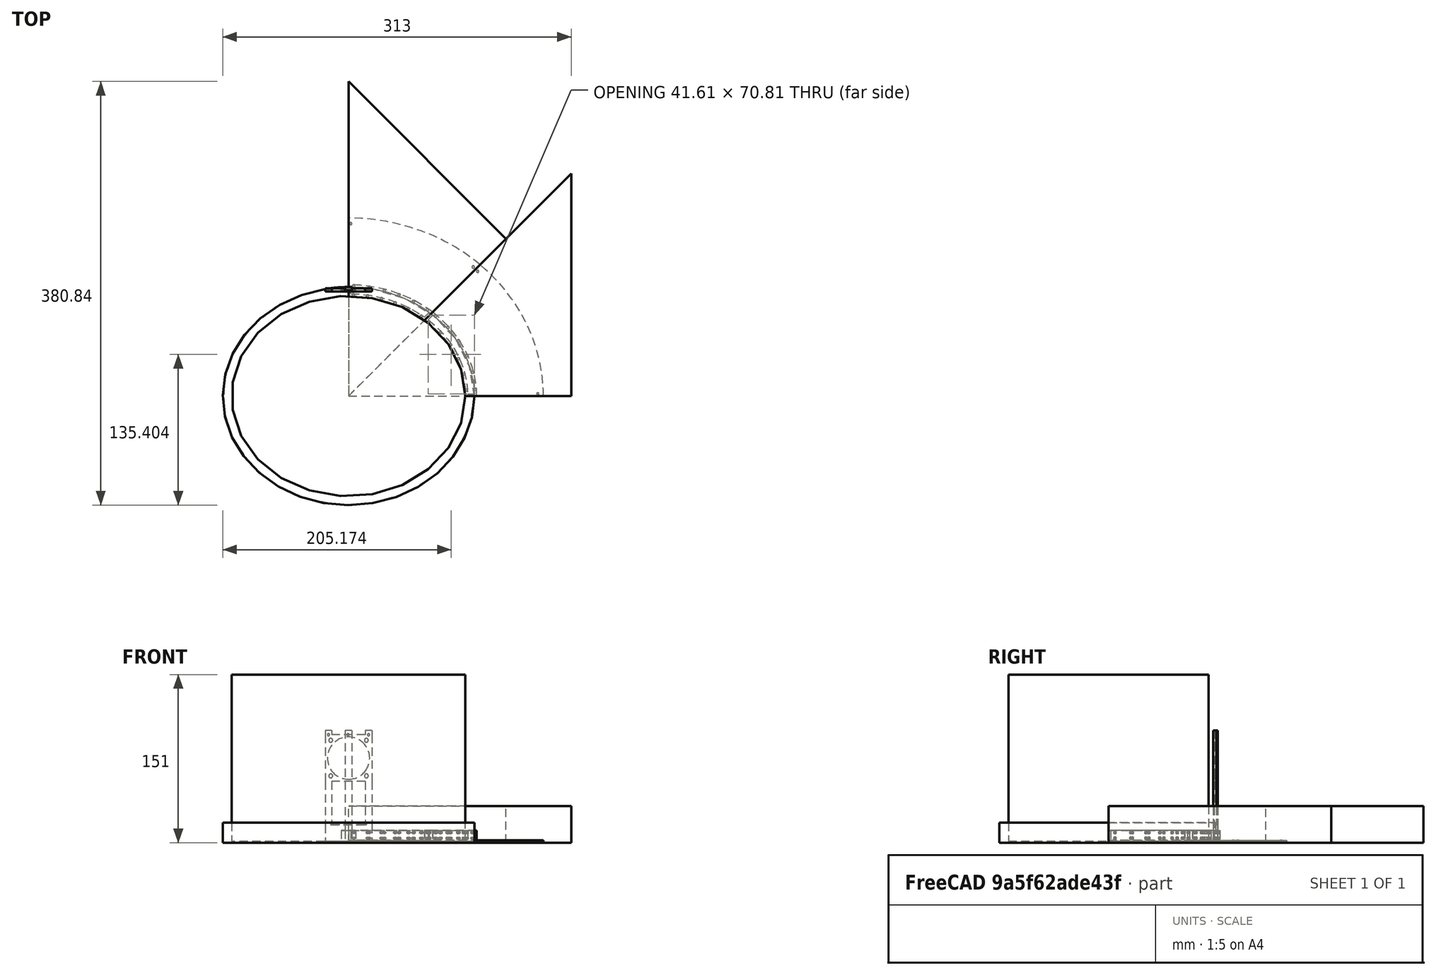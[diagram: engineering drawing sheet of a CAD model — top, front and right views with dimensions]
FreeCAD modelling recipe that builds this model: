
FCSTD DOCUMENT  (FreeCAD 0.14R3702 (Git))
Label: sun-hat-2
License: CC-BY 3.0
LicenseURL: http://creativecommons.org/licenses/by/3.0/
objects: Part::Cut×41, Part::Feature×16, Part::Cylinder×14, Part::Box×12, Part::Extrusion×8, Part::Fuse×6, Part::Ellipse×5, Part::MultiCommon×4, App::DocumentObjectGroup×1
note: 106 computed .brp shape members not serialized (recipe doc carries the construction recipe); baked Part::Feature solids carry a one-line shape summary decoded from their .brp

FEATURE [Part::Ellipse] Ellipse
  Angle0 = 0
  Angle1 = 360
  MajorRadius = 105
  MinorRadius = 90
FEATURE [Part::Ellipse] Ellipse001
  Angle0 = 0
  Angle1 = 360
  MajorRadius = 107
  MinorRadius = 92
FEATURE [Part::Ellipse] Ellipse002
  Angle0 = 0
  Angle1 = 360
  MajorRadius = 113
  MinorRadius = 98
FEATURE [Part::Ellipse] Ellipse003
  Angle0 = 0
  Angle1 = 360
  MajorRadius = 115
  MinorRadius = 100
FEATURE [Part::Feature] Face
  shape: bbox 210 x 180 x 2e-07 mm, 1 faces, 0 solids (baked)
FEATURE [Part::Feature] Face001
  shape: bbox 214 x 184 x 2e-07 mm, 1 faces, 0 solids (baked)
FEATURE [Part::Feature] Face002
  shape: bbox 226 x 196 x 2e-07 mm, 1 faces, 0 solids (baked)
FEATURE [Part::Feature] Face003
  shape: bbox 230 x 200 x 2e-07 mm, 1 faces, 0 solids (baked)
FEATURE [Part::Extrusion] Extrude  label="innermost+"
  Base = -> Face001
  Dir = (0,0,20)
  Placement = pos=(0,0,-1) rot=(0,0,1;0rad)
  Solid = false
FEATURE [Part::Extrusion] Extrude001  label="outermost-"
  Base = -> Face002
  Dir = (0,0,18)
  Solid = false
FEATURE [Part::Extrusion] Extrude002  label="innermost"
  Base = -> Face
  Dir = (0,0,150)
  Placement = pos=(0,0,-1) rot=(0,0,1;0rad)
  Solid = false
FEATURE [Part::Extrusion] Extrude003  label="outermost"
  Base = -> Face003
  Dir = (0,0,10)
  Solid = false
FEATURE [Part::Extrusion] Extrude004  label="central ellipse"
  Base = -> Face
  Dir = (0,0,150)
  Solid = false
FEATURE [Part::Cylinder] Cylinder
  Angle = 360
  Height = 150
  Placement = pos=(0,0,8) rot=(0,1,0;1.5708rad)
  Radius = 1
FEATURE [Part::Cylinder] Cylinder001
  Angle = 360
  Height = 150
  Placement = pos=(0,0,3) rot=(0,1,0;1.5708rad)
  Radius = 1
FEATURE [Part::Ellipse] Ellipse004
  Angle0 = 0
  Angle1 = 360
  MajorRadius = 175
  MinorRadius = 160
FEATURE [Part::Feature] Face004
  shape: bbox 350 x 320 x 2e-07 mm, 1 faces, 0 solids (baked)
FEATURE [Part::Extrusion] Extrude005  label="brim"
  Base = -> Face004
  Dir = (0,0,1)
  Solid = false
FEATURE [Part::Extrusion] Extrude006
  Base = -> Face002
  Dir = (0,0,18)
  Placement = pos=(0,0,-1) rot=(0,0,1;0rad)
  Solid = false
FEATURE [Part::Box] Box008  label="Cube001"
  Height = 33
  Length = 200
  Placement = pos=(0,0,-1) rot=(0,0,1;0rad)
  Width = 200
FEATURE [Part::Cylinder] Cylinder002
  Angle = 360
  Height = 10
  Placement = pos=(170,2,-1) rot=(0,0,1;0rad)
  Radius = 1
FEATURE [Part::Cylinder] Cylinder003
  Angle = 360
  Height = 10
  Placement = pos=(2,155,-1) rot=(0,0,1;0rad)
  Radius = 1
FEATURE [Part::Box] Box  label="Cube002"
  Height = 37
  Length = 313
  Placement = pos=(0,0,-2) rot=(0,0,1;0.785398rad)
  Width = 200
FEATURE [Part::Box] Box009  label="Cube003"
  Height = 37
  Length = 200
  Placement = pos=(0,0,-3) rot=(0,0,1;0rad)
  Width = 200
FEATURE [Part::Box] Box010  label="Cube004"
  Height = 43
  Length = 313
  Placement = pos=(0,0,-4) rot=(0,0,1;0.785398rad)
  Width = 200
FEATURE [Part::Cut] Cut  label="long-45"
  Base = -> Box008
  Tool = -> Box
FEATURE [Part::Cut] Cut001  label="spoke-a"
  Base = -> Box009
  Placement = pos=(4.828,2,0) rot=(0,0,1;0rad)
  Tool = -> Box010
FEATURE [Part::Cut] Cut002  label="short-45"
  Base = -> Box008
  Placement = pos=(0,0,0) rot=(0,0,1;0.785398rad)
  Tool = -> Box
FEATURE [Part::Cut] Cut003  label="spoke-b"
  Base = -> Box009
  Placement = pos=(2,4.828,0) rot=(0,0,1;0.785398rad)
  Tool = -> Box010
FEATURE [Part::Cut] Cut004  label="air-gap"
  Base = -> Extrude001
  Tool = -> Extrude
FEATURE [Part::Fuse] Fusion059  label="brim+outer"
  Base = -> Extrude003
  Tool = -> Extrude005
FEATURE [Part::Cut] Cut005
  Base = -> Fusion059
  Tool = -> Extrude002
FEATURE [Part::Cut] Cut006  label="long-45a"
  Base = -> Box008
  Tool = -> Box
FEATURE [Part::Cut] Cut007  label="short-45a"
  Base = -> Box008
  Placement = pos=(0,0,0) rot=(0,0,1;0.785398rad)
  Tool = -> Box
FEATURE [App::DocumentObjectGroup] Group  label="Construction"
  Group = -> [Ellipse,Ellipse001,Ellipse002,Ellipse003,Extrude004,Ellipse004,Extrude006,Cut006,Cut007]
FEATURE [Part::MultiCommon] Common  label="long-45-brim"
  Shapes = -> [Cut005,Cut]
FEATURE [Part::Cut] Cut008
  Base = -> Fusion059
  Tool = -> Extrude002
FEATURE [Part::MultiCommon] Common001  label="short-45-brim"
  Shapes = -> [Cut008,Cut002]
FEATURE [Part::Cut] Cut009  label="air-gap001"
  Base = -> Extrude001
  Tool = -> Extrude
FEATURE [Part::MultiCommon] Common002
  Shapes = -> [Cut004,Cut003]
FEATURE [Part::MultiCommon] Common003
  Shapes = -> [Cut009,Cut001]
FEATURE [Part::Cut] Cut010
  Base = -> Common001
  Tool = -> Common002
FEATURE [Part::Cut] Cut011
  Base = -> Common
  Tool = -> Common003
FEATURE [Part::Fuse] Fusion
  Base = -> Cylinder
  Placement = pos=(0,0,0) rot=(0,0,1;0.05236rad)
  Tool = -> Cylinder001
FEATURE [Part::Feature] Fusion060
  Placement = pos=(0,0,0) rot=(0,0,1;0.190532rad)
  shape: bbox 147.7 x 30.37 x 7 mm, 6 faces, 2 solids (baked)
FEATURE [Part::Feature] Fusion061
  Placement = pos=(0,0,0) rot=(0,0,1;0.328704rad)
  shape: bbox 142.6 x 50.32 x 7 mm, 6 faces, 2 solids (baked)
FEATURE [Part::Feature] Fusion062
  Placement = pos=(0,0,0) rot=(0,0,1;0.466876rad)
  shape: bbox 134.8 x 69.3 x 7 mm, 6 faces, 2 solids (baked)
FEATURE [Part::Feature] Fusion063
  Placement = pos=(0,0,0) rot=(0,0,1;0.605047rad)
  shape: bbox 124.5 x 86.97 x 7 mm, 6 faces, 2 solids (baked)
FEATURE [Part::Feature] Fusion064
  Placement = pos=(0,0,0) rot=(0,0,1;0.830485rad)
  shape: bbox 102.7 x 112.1 x 7 mm, 6 faces, 2 solids (baked)
FEATURE [Part::Feature] Fusion065
  Placement = pos=(0,0,0) rot=(0,0,1;0.743219rad)
  shape: bbox 111.8 x 103 x 7 mm, 6 faces, 2 solids (baked)
FEATURE [Part::Cut] Cut012
  Base = -> Cut011
  Tool = -> Fusion
FEATURE [Part::Cut] Cut013
  Base = -> Cut012
  Tool = -> Fusion060
FEATURE [Part::Cut] Cut014
  Base = -> Cut013
  Tool = -> Fusion061
FEATURE [Part::Cut] Cut015
  Base = -> Cut014
  Tool = -> Fusion062
FEATURE [Part::Cut] Cut016
  Base = -> Cut015
  Tool = -> Fusion063
FEATURE [Part::Cut] Cut017
  Base = -> Cut016
  Tool = -> Fusion065
FEATURE [Part::Feature] Fusion066
  Placement = pos=(0,0,0) rot=(0,0,1;0.968657rad)
  shape: bbox 86.61 x 124.8 x 7 mm, 6 faces, 2 solids (baked)
FEATURE [Part::Feature] Fusion067
  Placement = pos=(0,0,0) rot=(0,0,1;1.10683rad)
  shape: bbox 68.91 x 135 x 7 mm, 6 faces, 2 solids (baked)
FEATURE [Part::Feature] Fusion068
  Placement = pos=(0,0,0) rot=(0,0,1;1.245rad)
  shape: bbox 49.9 x 142.7 x 7 mm, 6 faces, 2 solids (baked)
FEATURE [Part::Feature] Fusion069
  Placement = pos=(0,0,0) rot=(0,0,1;1.38317rad)
  shape: bbox 29.94 x 147.7 x 7 mm, 6 faces, 2 solids (baked)
FEATURE [Part::Feature] Fusion070
  Placement = pos=(0,0,0) rot=(0,0,1;1.52134rad)
  shape: bbox 9.412 x 149.9 x 7 mm, 6 faces, 2 solids (baked)
FEATURE [Part::Cut] Cut018
  Base = -> Cut010
  Tool = -> Fusion064
FEATURE [Part::Cut] Cut019
  Base = -> Cut018
  Tool = -> Fusion070
FEATURE [Part::Cut] Cut020
  Base = -> Cut019
  Tool = -> Fusion069
FEATURE [Part::Cut] Cut021
  Base = -> Cut020
  Tool = -> Fusion068
FEATURE [Part::Cut] Cut022
  Base = -> Cut021
  Tool = -> Fusion067
FEATURE [Part::Cut] Cut023
  Base = -> Cut022
  Tool = -> Fusion066
FEATURE [Part::Cylinder] Cylinder004
  Angle = 360
  Height = 10
  Placement = pos=(112,116,-7) rot=(0,0,1;0rad)
  Radius = 1.1
FEATURE [Part::Cylinder] Cylinder005
  Angle = 360
  Height = 10
  Placement = pos=(116,112,-1) rot=(0,0,1;0rad)
  Radius = 1
FEATURE [Part::Cut] Cut024
  Base = -> Cut017
  Tool = -> Cylinder002
FEATURE [Part::Cut] Cut025
  Base = -> Cut023
  Tool = -> Cylinder003
FEATURE [Part::Cut] Cut026  label="front"
  Base = -> Cut024
  Tool = -> Cylinder005
FEATURE [Part::Cut] Cut027  label="side"
  Base = -> Cut025
  Tool = -> Cylinder004
FEATURE [Part::Box] Box011  label="Cube"
  Height = 3
  Length = 42
  Placement = pos=(-17,-21,0) rot=(0,0,1;0rad)
  Width = 42
FEATURE [Part::Cylinder] Cylinder006
  Angle = 360
  Height = 10
  Placement = pos=(4,0,-2) rot=(0,0,1;0rad)
  Radius = 19
FEATURE [Part::Cylinder] Cylinder007
  Angle = 360
  Height = 10
  Placement = pos=(20,-16,-1) rot=(0,0,1;0rad)
  Radius = 1.75
FEATURE [Part::Cylinder] Cylinder008
  Angle = 360
  Height = 10
  Placement = pos=(-12,-16,-1) rot=(0,0,1;0rad)
  Radius = 1.75
FEATURE [Part::Cylinder] Cylinder010
  Angle = 360
  Height = 10
  Placement = pos=(-12,16,-1) rot=(0,0,1;0rad)
  Radius = 1.75
FEATURE [Part::Box] Box018  label="Cube011"
  Height = 3
  Length = 100
  Placement = pos=(-21,-21,0) rot=(0,0,1;0rad)
  Width = 6
FEATURE [Part::Box] Box020  label="Cube013"
  Height = 5
  Length = 15
  Placement = pos=(64,-21,0) rot=(0,0,1;0rad)
  Width = 42
FEATURE [Part::Extrusion] Extrude007  label="outermost-001"
  Base = -> Face002
  Dir = (0,0,18)
  Solid = false
FEATURE [Part::Box] Box021  label="Cube014"
  Height = 17
  Length = 47
  Placement = pos=(-22,95,0.5) rot=(0,0,1;0rad)
  Width = 10
FEATURE [Part::Box] Box022  label="Cube015"
  Height = 11
  Length = 6
  Placement = pos=(-3,90,-1) rot=(0,0,1;0rad)
  Width = 10
FEATURE [Part::Cut] Cut033
  Base = -> Box021
  Placement = pos=(0,0,-1) rot=(0,0,1;0rad)
  Tool = -> Extrude007
FEATURE [Part::Cylinder] Cylinder009
  Angle = 360
  Height = 10
  Placement = pos=(20,16,-1) rot=(0,0,1;0rad)
  Radius = 1.75
FEATURE [Part::Box] Box023  label="Cube016"
  Height = 3
  Length = 100
  Placement = pos=(-21,15,0) rot=(0,0,1;0rad)
  Width = 6
FEATURE [Part::Fuse] Fusion071
  Base = -> Box018
  Tool = -> Box023
FEATURE [Part::Fuse] Fusion072
  Base = -> Box011
  Tool = -> Fusion071
FEATURE [Part::Fuse] Fusion073
  Base = -> Box020
  Tool = -> Fusion072
FEATURE [Part::Cut] Cut034
  Base = -> Fusion073
  Tool = -> Cylinder008
FEATURE [Part::Cut] Cut035
  Base = -> Cut034
  Tool = -> Cylinder006
FEATURE [Part::Cut] Cut036
  Base = -> Cut035
  Tool = -> Cylinder007
FEATURE [Part::Cut] Cut037
  Base = -> Cut036
  Tool = -> Cylinder010
FEATURE [Part::Cut] Cut038
  Base = -> Cut037
  Tool = -> Cylinder009
FEATURE [Part::Box] Box024  label="Cube017"
  Height = 3
  Length = 100
  Placement = pos=(-21,-21,0) rot=(0,0,1;0rad)
  Width = 6
FEATURE [Part::Cylinder] Cylinder011
  Angle = 360
  Height = 10
  Placement = pos=(-17,-18,-1) rot=(0,0,1;0rad)
  Radius = 1
FEATURE [Part::Cylinder] Cylinder012
  Angle = 360
  Height = 10
  Placement = pos=(-17,-17.5,-1) rot=(0,0,1;0rad)
  Radius = 1
FEATURE [Part::Cylinder] Cylinder013
  Angle = 360
  Height = 10
  Placement = pos=(-17,18,-1) rot=(0,0,1;0rad)
  Radius = 1
FEATURE [Part::Cut] Cut039
  Base = -> Cut038
  Tool = -> Cylinder011
FEATURE [Part::Cut] Cut040
  Base = -> Cut039
  Placement = pos=(0,94,79) rot=(-0.57735,0.57735,0.57735;2.0944rad)
  Tool = -> Cylinder013
FEATURE [Part::Cut] Cut041
  Base = -> Box021
  Placement = pos=(0,0,-1) rot=(0,0,1;0rad)
  Tool = -> Extrude007
FEATURE [Part::Cut] Cut042
  Base = -> Cut040
  Tool = -> Cut033
FEATURE [Part::Cut] Cut043  label="fan-holder"
  Base = -> Cut042
  Tool = -> Box022
FEATURE [Part::Cut] Cut044
  Base = -> Box024
  Tool = -> Cylinder012
FEATURE [Part::Box] Box025  label="Cube018"
  Height = 10
  Length = 10
  Placement = pos=(69,-24.5,0) rot=(0,0,1;0rad)
  Width = 13
FEATURE [Part::Fuse] Fusion074
  Base = -> Cut044
  Placement = pos=(-18,95,79) rot=(-0.57735,0.57735,0.57735;2.0944rad)
  Tool = -> Box025
FEATURE [Part::Cut] Cut045  label="vertical"
  Base = -> Fusion074
  Tool = -> Cut041
